# Revit family: Faucet_Vessel-Lavatory-DXV-Rem-D3510015X_Series
name_source: partatom
category: Plumbing Fixtures
revit_build: Autodesk Revit 2014 (Build: 20130308_1515(x64)
units: mm (PartAtom-declared; Revit-internal decimal feet)

## types (4) — shared parameters
ADA Compliant = Yes
Assembly Code = D2020300
CW Connection = Yes
CWFU = 1.5
Cold Water Connection Diameter = 3/8"
Default Elevation = 0"
Description = REM Vessel Faucets
HW Connection = Yes
HWFU = 1.5
Height = 11 7/8"
Hot Water Connection Diameter = 0"
Installation Type = Deck Mounted
Length = 6"
Manufacturer = DXV
Price = Prices may vary. Please consult Manufacturer Representative for most up-to-date price list.
Product Documentation Link = https://dxv01.blob.core.windows.net
Product Page URL = https://www.dxv.com
Revised Date = 27/09/2017
URL = http://www.dxv.com
Vent Connection = No
WFU = 2
Warranty Documentation Link = https://www.dxv.com
Waste Connection = No
Width = 2"

## per-type parameters (varying)
| type | Finish | Flow Rate | Material |
| D35100150.100 | Metal-DXV-100-Polished Chrome | 1.5 GPM (5.7 L/min.) | Metal-DXV-100-Polished Chrome |
| D35100150.144 | Metal-DXV-144-Brushed Nickel | 1.5 GPM (5.7 L/min.) | Metal-DXV-144-Brushed Nickel |
| D3510015C.100 | Metal-DXV-100-Polished Chrome | 1.2 GPM (4.5 L/min.) | Metal-DXV-100-Polished Chrome |
| D3510015C.144 | Metal-DXV-144-Brushed Nickel | 1.2 GPM (4.5 L/min.) | Metal-DXV-144-Brushed Nickel |

note: column(s) folded — value = type name in every type: Model

## geometry (parser evidence)
native form markers: Sweep x1
no freeform markers — native parametric forms only
